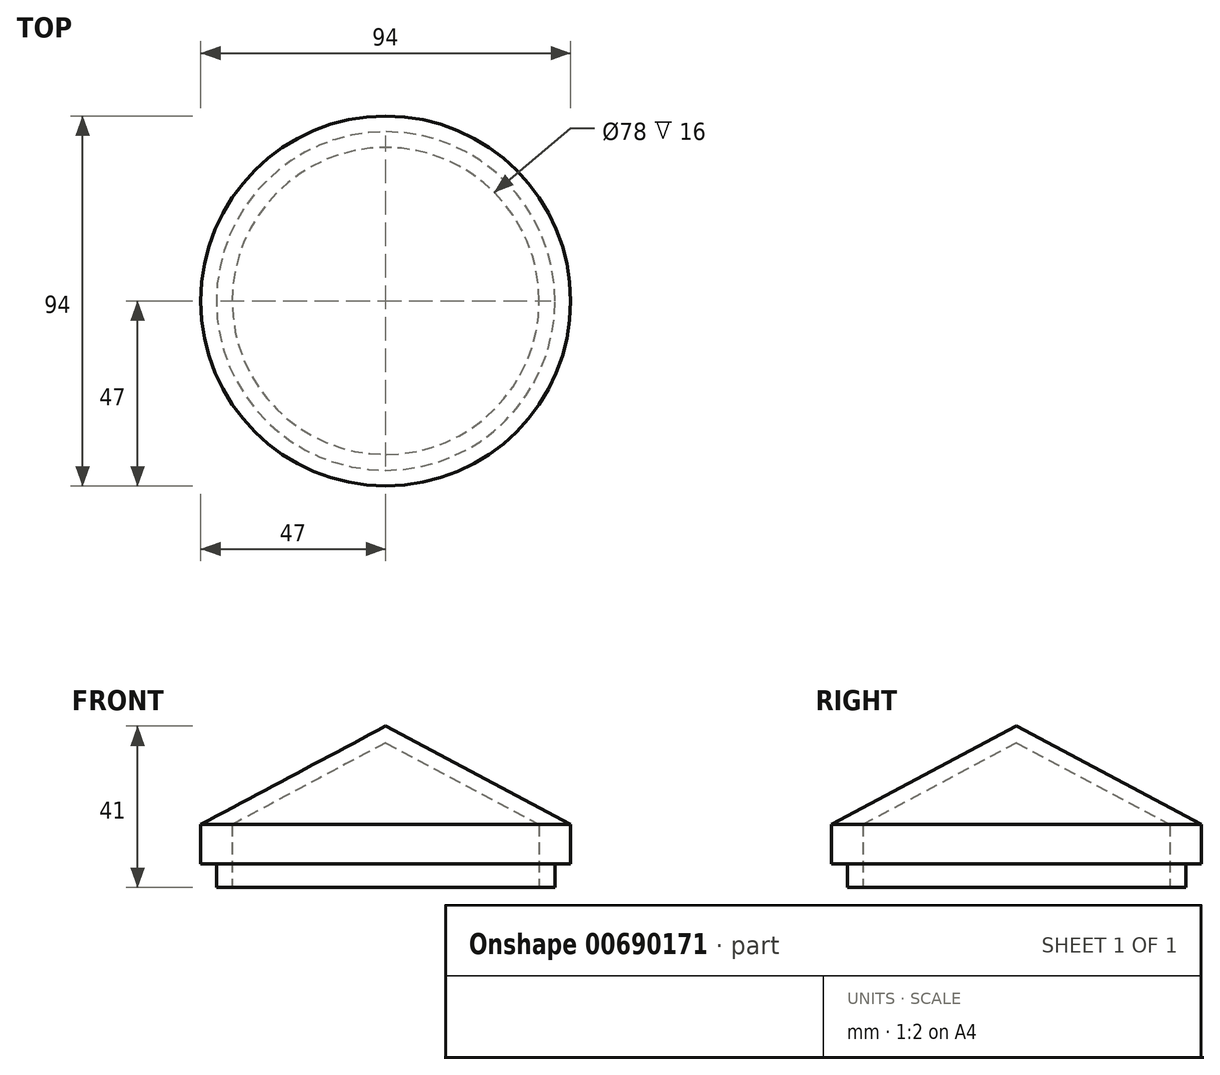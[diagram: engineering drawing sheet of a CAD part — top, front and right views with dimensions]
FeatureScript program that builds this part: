
annotation { "Feature Type Name" : "Feature", "Feature Type Description" : "" }
export const myFeature = defineFeature(function(context is Context, id is Id, definition is map)
    precondition{}
    {
        {
            var Q0;
            Q0=qCreatedBy(makeId("Top.planeOp"),FACE);
            var sketch = newSketch(context, id + "F0", { "sketchPlane" : qUnion([Q0])});
            skCircle(sketch, "E0", {"center": v(0, 0) * mm, "radius": 47 * mm});
            skSolve(sketch);
        }
        {
            var Q0;
            Q0 = qSketchRegion(id + "F0", true);
            extrude(context, id + "F1", {"entities" : qUnion([Q0]), "depth" : 16 * mm, "offsetDistance" : 25 * mm});
        }
        {
            var Q0;
            Q0=makeQuery(id+"F1.opExtrude","CAP_FACE",FACE,{"disambiguationData":[OSD([sQuery(id+"F0.wireOp",EDGE,"E0")])],"isStart":true});
            var sketch = newSketch(context, id + "F2", { "sketchPlane" : qUnion([Q0])});
            skCircle(sketch, "E1", {"center": v(0, 0) * mm, "radius": 39 * mm});
            skSolve(sketch);
        }
        {
            var Q0;
            Q0 = qSketchRegion(id + "F2", true);
            extrude(context, id + "F3", {"entities" : qUnion([Q0]), "operationType" : NewBodyOperationType.REMOVE, "oppositeDirection" : true, "depth" : 16 * mm, "offsetDistance" : 25 * mm});
        }
        {
            var Q0;
            Q0=makeQuery(id+"F1.opExtrude","CAP_FACE",FACE,{"disambiguationData":[OSD([sQuery(id+"F0.wireOp",EDGE,"E0")])],"isStart":true});
            var sketch = newSketch(context, id + "F4", { "sketchPlane" : qUnion([Q0])});
            skCircle(sketch, "E2", {"center": v(0, 0) * mm, "radius": 43 * mm});
            skCircle(sketch, "E3", {"center": v(0, 0) * mm, "radius": 47 * mm});
            skSolve(sketch);
        }
        {
            var Q0;
            Q0 = qSketchRegion(id + "F4", true);
            extrude(context, id + "F5", {"entities" : qUnion([Q0]), "operationType" : NewBodyOperationType.REMOVE, "oppositeDirection" : true, "depth" : 6 * mm, "offsetDistance" : 25 * mm});
        }
        {
            var Q0;
            Q0=qCreatedBy(makeId("Front.planeOp"),FACE);
            var sketch = newSketch(context, id + "F6", { "sketchPlane" : qUnion([Q0])});
            skLineSegment(sketch, "E4", {"start": v(0, 0) * mm, "end": v(0, 24.3) * mm});
            skSolve(sketch);
        }
        {
            var Q0;
            Q0=qCreatedBy(makeId("Front.planeOp"),FACE);
            var sketch = newSketch(context, id + "F7", { "sketchPlane" : qUnion([Q0])});
            skLineSegment(sketch, "E5", {"start": v(0, 36.74) * mm, "end": v(0, 41) * mm});
            skLineSegment(sketch, "E6", {"start": v(0, 41) * mm, "end": v(-47, 16) * mm});
            skLineSegment(sketch, "E7", {"start": v(-47, 16) * mm, "end": v(-39, 16) * mm});
            skLineSegment(sketch, "E8", {"start": v(-39, 16) * mm, "end": v(0, 36.74) * mm});
            skSolve(sketch);
        }
        {
            var Q0;
            Q0=makeQuery(id+"F7.imprint","IMPRINT",FACE,{"disambiguationData":[TD([[makeQuery(id+"F7.imprint","IMPRINT",EDGE,{"derivedFrom":sQuery(id+"F7.wireOp",EDGE,"E5")}),1.0]])]});
            var Q1;
            Q1=sQuery(id+"F6.wireOp",EDGE,"E4");
            revolve(context, id + "F8", {"operationType" : NewBodyOperationType.ADD, "surfaceOperationType" : NewSurfaceOperationType.NEW, "entities" : qUnion([Q0]), "axis" : qUnion([Q1]), "revolveType" : RevolveType.FULL});
        }
    });
